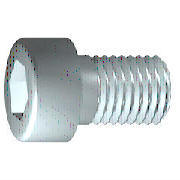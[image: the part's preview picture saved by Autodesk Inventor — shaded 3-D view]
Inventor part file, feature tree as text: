
AUTODESK INVENTOR PART (.ipt)
format: ipt  version: 2020 (Build 240168000, 168)  size: 201,728 bytes
history: native  units: mm (DEFAULTED — no unit token found)
features: sketch x2, extrude x1, plane x1, fillet x1
ambient origin geometry x7: Origin, YZ Plane, XY Plane, X Axis, Y Axis, Z Axis, Center Point
bodies: Solid1 (feature_tree), Body (feature_tree)
feature tree (5):
  extrude  "Slot"  Depth=3.5mm
  plane  "Work Plane1"
  fillet  "Fillet2"  Radius=3.5mm
  sketch  "Sketch1"  dims[d1=5.6mm d2=0.49086mm d3=3.5mm]
  sketch  "Sketch2"  dims[d4=2.7mm d5=60.0deg d6=5.0mm d7=5.0mm d8=3.464102mm d9=8.5mm d10=90.0deg d11=10.0mm d12=0.0mm d13=5.6mm d14=0.0mm d15=0.49076mm d16=0.49076mm d17=0.5mm d19=0.0mm d26=8.0mm d27=45.0deg d28=0.0mm d29=0.0mm d30=0.1mm]
